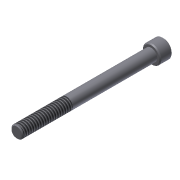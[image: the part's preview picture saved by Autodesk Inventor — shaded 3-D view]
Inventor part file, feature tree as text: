
AUTODESK INVENTOR PART (.ipt)
format: ipt  version: 2013 (Build 170138000, 138)  size: 99,840 bytes
history: native  units: in
note: dims shown in document units (in); Inventor stores cm internally (conversion verified against a paired STEP export)
features: extrude x3, sketch x3, chamfer x1, thread x1
ambient origin geometry x8: Origin, YZ Plane, XZ Plane, XY Plane, X Axis, Y Axis, Z Axis, Center Point
bodies: Solid1 (feature_tree)
feature tree (8):
  extrude  "Extrusion1"  Depth=2.75in TaperAngle=0.0deg
  extrude  "Extrusion2"  Depth=0.25in TaperAngle=0.0deg
  extrude  "Extrusion3"  Depth=0.125in TaperAngle=0.0deg
  chamfer  "Chamfer1"  Distance=0.02in Angle=45.0deg
  thread  "Thread1"  [1 undecoded]
  sketch  "Sketch1"  dims[d0=0.25in d1=2.75in d2=0.0in]
  sketch  "Sketch2"  dims[d3=0.375in d4=0.25in d5=0.0in]
  sketch  "Sketch3"  dims[d6=0.1875in d7=0.125in d8=0.0in d9=0.02in d10=0.125in d11=45.0deg d12=1.0in d13=0.0in]
note: 1 required parameter value undecoded (feature->parameter linkage not recoverable at this tier; creation-order binding heuristic only, values carry confidence <= 0.55)
